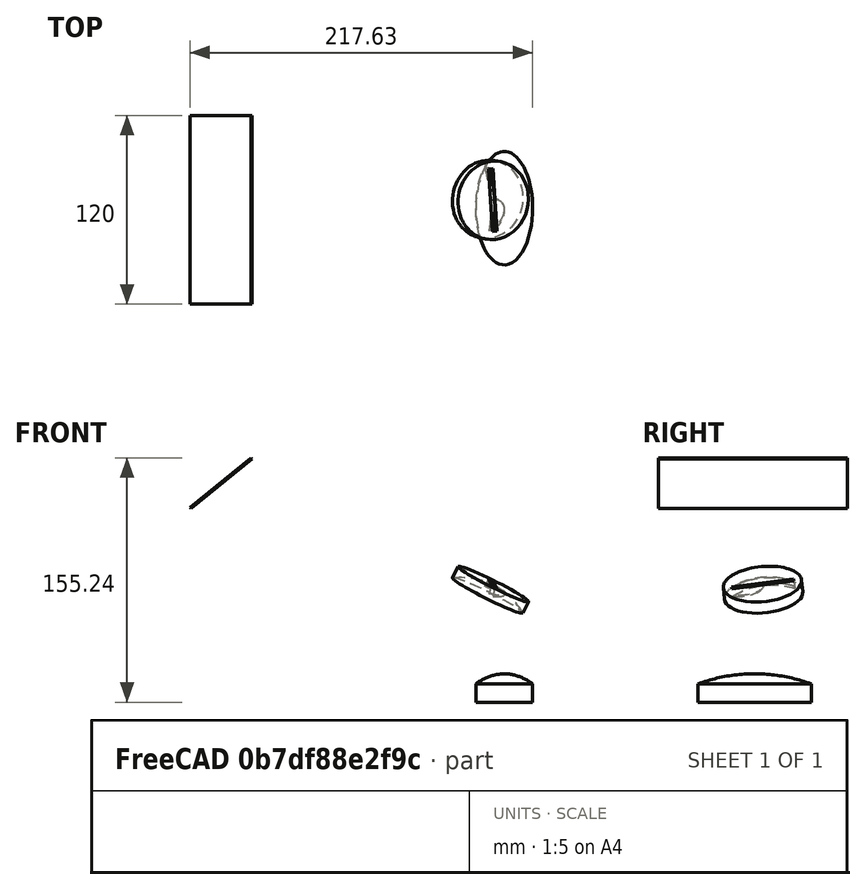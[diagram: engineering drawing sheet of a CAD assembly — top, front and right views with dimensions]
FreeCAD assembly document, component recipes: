
FREECAD ASSEMBLY — COMPONENT RECIPES ("main")

This assembly document has 3 components, labeled P0..P2 below (a component is one placed body or linked part). 1 of them carries a construction recipe — the FreeCAD feature program that regenerates the part from scratch, quoted from this document or its linked companion documents; the rest are supplied as boundary geometry only. No exploded tour is included for this assembly.
COMPONENT P0 — recipe-attached ("detector", modeled in this document).
Construction recipe (the document's own serialized feature program — sketch geometry with constraints, then the solid features built on it; lengths are millimeters unless a unit is written):

FEATURE [PartDesign::AdditiveBox] Box001
  AttacherType = Attacher::AttachEngine3D
  Height = 1
  Length = 50
  Refine = true
  Suppressed = false
  Width = 120
FEATURE [PartDesign::Body] Body  label="detector"
  AllowCompound = false
  Group = -> [Box001]
  Origin = -> Origin004
  Placement = pos=(-192,-66,137) rot=(0,1,0;-0.680678rad)
  Tip = -> Box001
COMPONENT P1 — geometry summary ("lens2"; no construction recipe available for this part):
  bounding box: 18.0 x 18.0 x 6.0 mm
  tessellated surface: 1,586 triangles
  volume: 1260 mm^3 (65% of its bounding box)
  symmetry: revolution-symmetric about the z axis through its bounding-box center; mirror-symmetric across its x mid-plane, y mid-plane
COMPONENT P2 — geometry summary ("slottedMirror"; no construction recipe available for this part):
  bounding box: 128.4 x 88.0 x 67.3 mm
  tessellated surface: 9,188 triangles
  volume: 16024 mm^3 (2% of its bounding box)
PROVENANCE & LICENSES
A FreeCAD (.FCStd) document from a public repository crawl; recipes are the document's own serialized feature recipes (and, for linked parts, companion documents' recipes).
License: lgpl-3.0.
